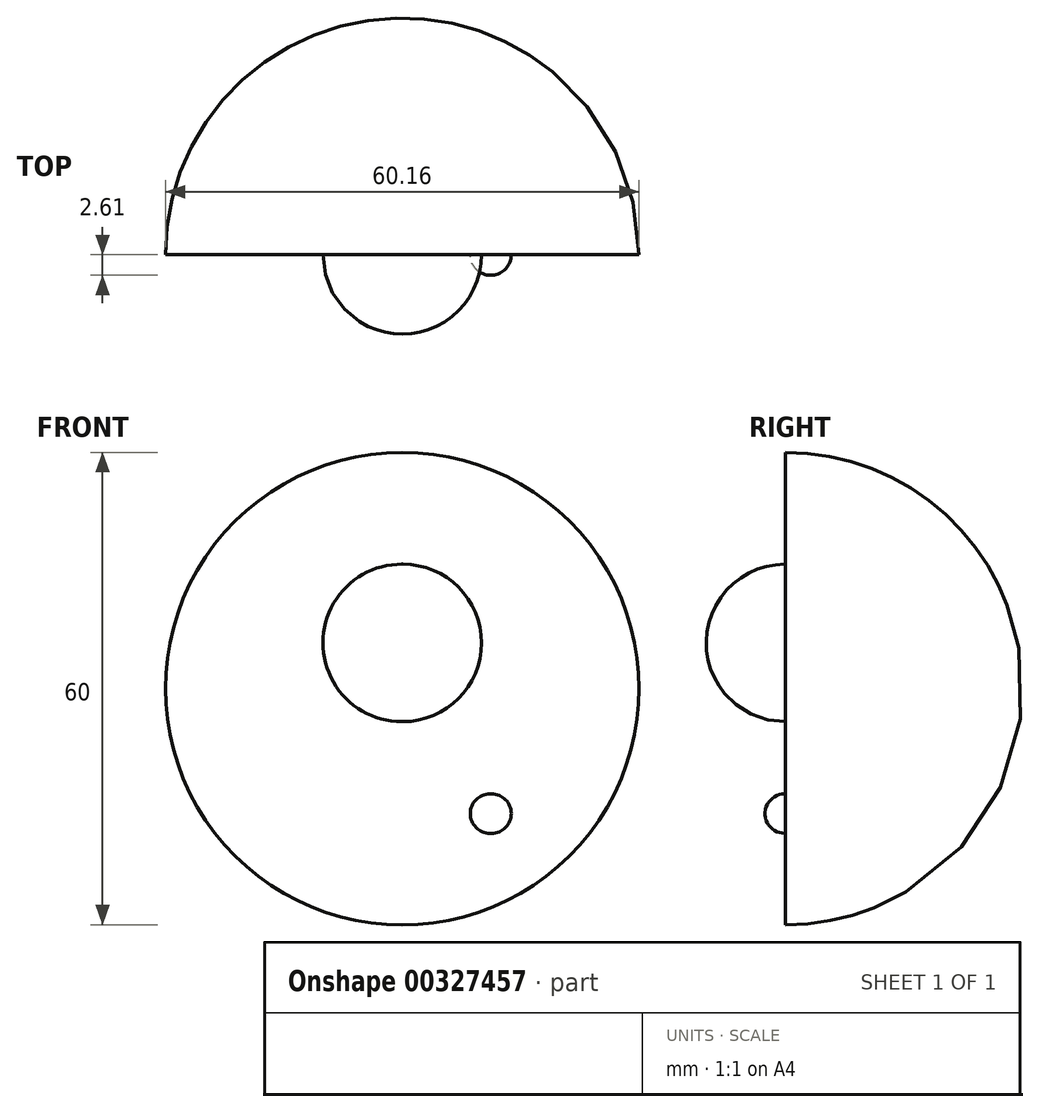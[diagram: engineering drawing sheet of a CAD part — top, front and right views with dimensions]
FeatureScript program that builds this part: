
annotation { "Feature Type Name" : "Feature", "Feature Type Description" : "" }
export const myFeature = defineFeature(function(context is Context, id is Id, definition is map)
    precondition{}
    {
        {
            var Q0;
            Q0=qCreatedBy(makeId("Front.planeOp"),FACE);
            var sketch = newSketch(context, id + "F0", { "sketchPlane" : qUnion([Q0])});
            skLineSegment(sketch, "E0", {"start": v(0, 0) * mm, "end": v(0, 60) * mm});
            skArc(sketch, "E1", {"start": v(0, 0) * mm, "mid": v(30.08, 30) * mm, "end": v(0, 60) * mm});
            skSolve(sketch);
        }
        {
            var Q0;
            Q0 = qSketchRegion(id + "F0", true);
            var Q1;
            Q1=sQuery(id+"F0.wireOp",EDGE,"E0");
            revolve(context, id + "F1", {"entities" : qUnion([Q0]), "axis" : qUnion([Q1]), "revolveType" : RevolveType.ONE_DIRECTION, "angle" : 180 * degree});
        }
        {
            var Q0;
            Q0=qCreatedBy(makeId("Front.planeOp"),FACE);
            var sketch = newSketch(context, id + "F2", { "sketchPlane" : qUnion([Q0])});
            skLineSegment(sketch, "E2", {"start": v(0, 25.8) * mm, "end": v(0, 45.8) * mm});
            skArc(sketch, "E3", {"start": v(0, 25.8) * mm, "mid": v(10.07, 35.8) * mm, "end": v(0, 45.8) * mm});
            skSolve(sketch);
        }
        {
            var Q0;
            Q0 = qSketchRegion(id + "F2", true);
            var Q1;
            Q1=sQuery(id+"F2.wireOp",EDGE,"E2");
            revolve(context, id + "F3", {"operationType" : NewBodyOperationType.ADD, "entities" : qUnion([Q0]), "axis" : qUnion([Q1]), "revolveType" : RevolveType.FULL});
        }
        {
            var Q0;
            Q0=qCreatedBy(makeId("Front.planeOp"),FACE);
            var sketch = newSketch(context, id + "F4", { "sketchPlane" : qUnion([Q0])});
            skEllipse(sketch, "E4", {"center": v(-23.4, 34.24) * mm, "majorRadius": 5.03 * mm, "minorRadius": 1.84 * mm, "majorAxis": v(0, -1)});
            skSolve(sketch);
        }
        {
            var Q0;
            Q0=sQuery(id+"F4.wireOp",EDGE,"E4");
            extrude(context, id + "F5", {"bodyType" : ToolBodyType.SURFACE, "surfaceEntities" : qUnion([Q0]), "endBound" : BoundingType.SYMMETRIC, "depth" : 5 * mm});
        }
        {
            var Q0;
            Q0=qCreatedBy(makeId("Front.planeOp"),FACE);
            var sketch = newSketch(context, id + "F6", { "sketchPlane" : qUnion([Q0])});
            skLineSegment(sketch, "E5", {"start": v(11.25, 16.62) * mm, "end": v(11.25, 11.62) * mm});
            skArc(sketch, "E6", {"start": v(11.25, 11.62) * mm, "mid": v(13.85, 14.12) * mm, "end": v(11.25, 16.62) * mm});
            skSolve(sketch);
        }
        {
            var Q0;
            Q0 = qSketchRegion(id + "F6", true);
            var Q1;
            Q1=sQuery(id+"F6.wireOp",EDGE,"E5");
            revolve(context, id + "F7", {"operationType" : NewBodyOperationType.ADD, "entities" : qUnion([Q0]), "axis" : qUnion([Q1]), "revolveType" : RevolveType.ONE_DIRECTION, "angle" : 180 * degree});
        }
    });
